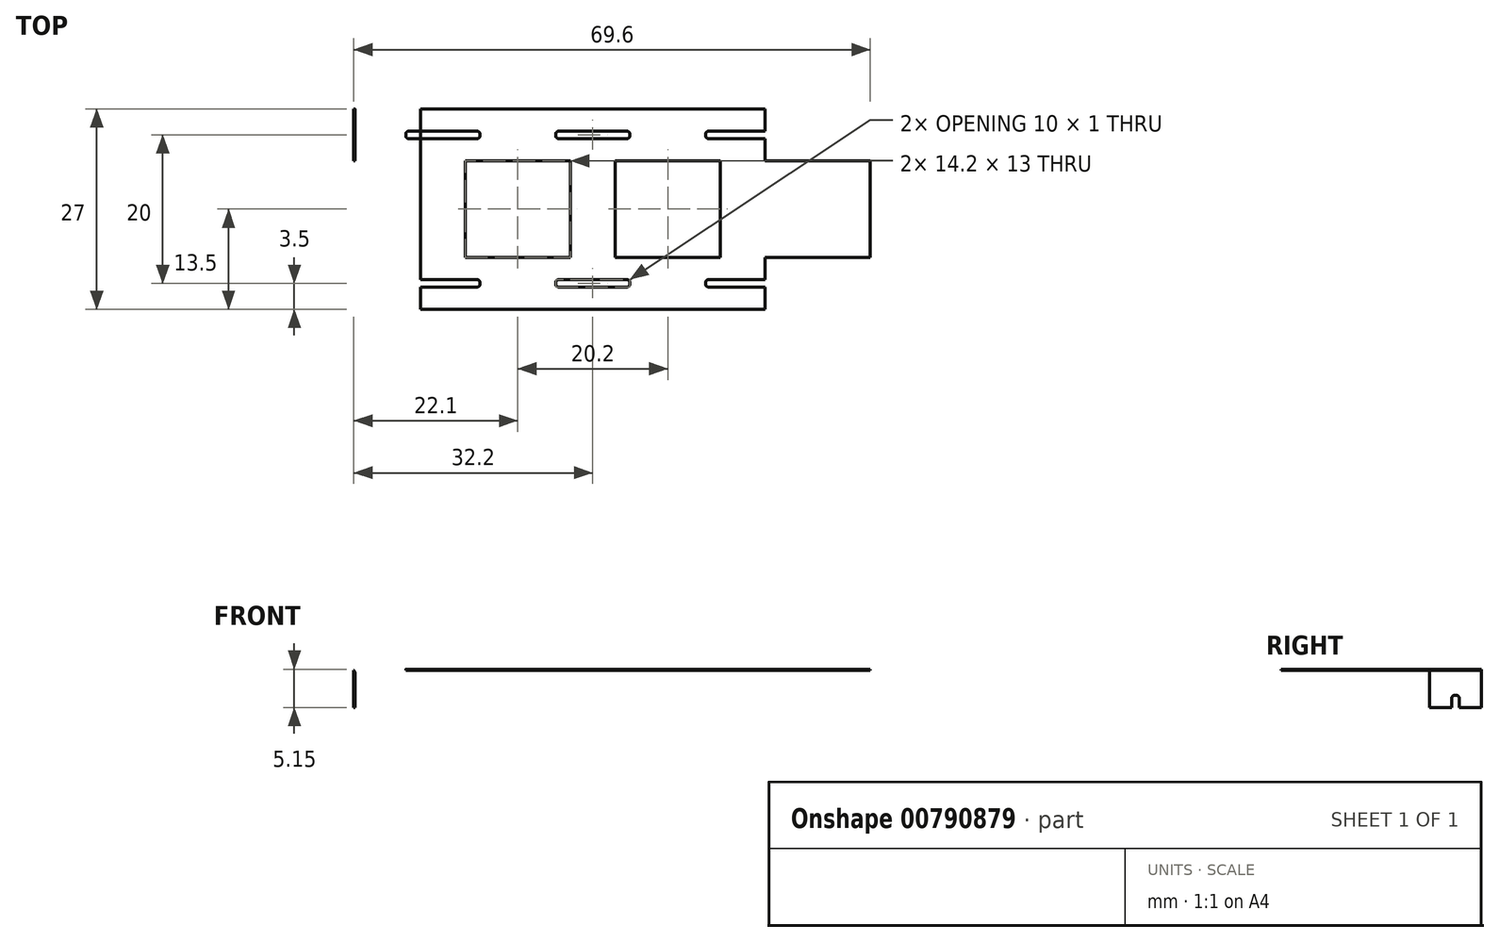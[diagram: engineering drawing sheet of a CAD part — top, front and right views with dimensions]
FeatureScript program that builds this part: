
annotation { "Feature Type Name" : "Feature", "Feature Type Description" : "" }
export const myFeature = defineFeature(function(context is Context, id is Id, definition is map)
    precondition{}
    {
        {
            var Q0;
            Q0=qCreatedBy(makeId("Top.planeOp"),FACE);
            var sketch = newSketch(context, id + "F0", { "sketchPlane" : qUnion([Q0])});
            skLineSegment(sketch, "E0.bottom", {"start": v(7.1, 6.5) * mm, "end": v(-7.1, 6.5) * mm});
            skLineSegment(sketch, "E0.top", {"start": v(7.1, -6.5) * mm, "end": v(-7.1, -6.5) * mm});
            skLineSegment(sketch, "E0.left", {"start": v(7.1, 6.5) * mm, "end": v(7.1, -6.5) * mm});
            skLineSegment(sketch, "E0.right", {"start": v(-7.1, 6.5) * mm, "end": v(-7.1, -6.5) * mm});
            skPoint(sketch, "E0.middle", {"position": v(0, 0) * mm});
            skLineSegment(sketch, "E1", {"start": v(13.1, 13.5) * mm, "end": v(13.1, 10.5) * mm});
            skLineSegment(sketch, "E2", {"start": v(13.1, 13.5) * mm, "end": v(-7.1, 13.5) * mm});
            skLineSegment(sketch, "E3.bottom", {"start": v(5.5, 9.5) * mm, "end": v(14.7, 9.5) * mm});
            skLineSegment(sketch, "E3.top", {"start": v(5.5, 10.5) * mm, "end": v(14.7, 10.5) * mm});
            skLineSegment(sketch, "E3.left", {"start": v(5.1, 9.9) * mm, "end": v(5.1, 10.1) * mm});
            skLineSegment(sketch, "E3.right", {"start": v(15.1, 9.9) * mm, "end": v(15.1, 10.1) * mm});
            skPoint(sketch, "E3.middle", {"position": v(10.1, 10) * mm});
            skPoint(sketch, "E4.visualSharp", {"position": v(5.1, 10.5) * mm});
            skArc(sketch, "E4.filletArc", {"start": v(5.5, 10.5) * mm, "mid": v(5.22, 10.38) * mm, "end": v(5.1, 10.1) * mm});
            skPoint(sketch, "E5.visualSharp", {"position": v(5.1, 9.5) * mm});
            skArc(sketch, "E5.filletArc", {"start": v(5.1, 9.9) * mm, "mid": v(5.22, 9.62) * mm, "end": v(5.5, 9.5) * mm});
            skPoint(sketch, "E6.visualSharp", {"position": v(15.1, 10.5) * mm});
            skArc(sketch, "E6.filletArc", {"start": v(15.1, 10.1) * mm, "mid": v(14.98, 10.38) * mm, "end": v(14.7, 10.5) * mm});
            skPoint(sketch, "E7.visualSharp", {"position": v(15.1, 9.5) * mm});
            skArc(sketch, "E7.filletArc", {"start": v(14.7, 9.5) * mm, "mid": v(14.98, 9.62) * mm, "end": v(15.1, 9.9) * mm});
            skLineSegment(sketch, "E8.trimOffspring", {"start": v(13.1, 9.5) * mm, "end": v(13.1, 0) * mm});
            skArc(sketch, "E9.MirrorCS", {"start": v(-5.5, 10.5) * mm, "mid": v(-5.22, 10.38) * mm, "end": v(-5.1, 10.1) * mm});
            skArc(sketch, "E10.MirrorCS", {"start": v(-15.1, 10.1) * mm, "mid": v(-14.98, 10.38) * mm, "end": v(-14.7, 10.5) * mm});
            skLineSegment(sketch, "E11.MirrorCS", {"start": v(-15.1, 9.9) * mm, "end": v(-15.1, 10.1) * mm});
            skArc(sketch, "E12.MirrorCS", {"start": v(-14.7, 9.5) * mm, "mid": v(-14.98, 9.62) * mm, "end": v(-15.1, 9.9) * mm});
            skArc(sketch, "E13.MirrorCS", {"start": v(-5.1, 9.9) * mm, "mid": v(-5.22, 9.62) * mm, "end": v(-5.5, 9.5) * mm});
            skLineSegment(sketch, "E14.MirrorCS", {"start": v(-5.1, 9.9) * mm, "end": v(-5.1, 10.1) * mm});
            skPoint(sketch, "E15.MirrorP", {"position": v(-5.1, 9.5) * mm});
            skLineSegment(sketch, "E16.MirrorCS", {"start": v(-5.5, 10.5) * mm, "end": v(-14.7, 10.5) * mm});
            skPoint(sketch, "E17.MirrorP", {"position": v(-10.1, 10) * mm});
            skLineSegment(sketch, "E18.MirrorCS", {"start": v(-5.5, 9.5) * mm, "end": v(-14.7, 9.5) * mm});
            skPoint(sketch, "E19.MirrorP", {"position": v(-15.1, 10.5) * mm});
            skLineSegment(sketch, "E20.MirrorCS", {"start": v(-13.1, 9.5) * mm, "end": v(-13.1, 0) * mm});
            skPoint(sketch, "E21.MirrorP", {"position": v(-5.1, 10.5) * mm});
            skLineSegment(sketch, "E22.MirrorCS", {"start": v(-13.1, 13.5) * mm, "end": v(-13.1, 10.5) * mm});
            skPoint(sketch, "E23.MirrorP", {"position": v(-15.1, 9.5) * mm});
            skLineSegment(sketch, "E24", {"start": v(-13.1, 13.5) * mm, "end": v(-7.1, 13.5) * mm});
            skLineSegment(sketch, "E25.bottom", {"start": v(-13.1, 13.5) * mm, "end": v(-22.1, 13.5) * mm});
            skLineSegment(sketch, "E25.top", {"start": v(-13.1, 6.5) * mm, "end": v(-22.1, 6.5) * mm});
            skLineSegment(sketch, "E25.left", {"start": v(-13.1, 13.5) * mm, "end": v(-13.1, 6.5) * mm});
            skLineSegment(sketch, "E25.right", {"start": v(-22.1, 13.5) * mm, "end": v(-22.1, 6.5) * mm});
            skArc(sketch, "E26.MirrorCS", {"start": v(14.7, -9.5) * mm, "mid": v(14.98, -9.62) * mm, "end": v(15.1, -9.9) * mm});
            skLineSegment(sketch, "E27.MirrorCS", {"start": v(15.1, -9.9) * mm, "end": v(15.1, -10.1) * mm});
            skArc(sketch, "E28.MirrorCS", {"start": v(15.1, -10.1) * mm, "mid": v(14.98, -10.38) * mm, "end": v(14.7, -10.5) * mm});
            skLineSegment(sketch, "E29.MirrorCS", {"start": v(13.1, -13.5) * mm, "end": v(13.1, -10.5) * mm});
            skLineSegment(sketch, "E30.MirrorCS", {"start": v(13.1, -9.5) * mm, "end": v(13.1, 0) * mm});
            skLineSegment(sketch, "E31.MirrorCS", {"start": v(13.1, -13.5) * mm, "end": v(-7.1, -13.5) * mm});
            skLineSegment(sketch, "E32.MirrorCS", {"start": v(5.5, -10.5) * mm, "end": v(14.7, -10.5) * mm});
            skPoint(sketch, "E33.MirrorP", {"position": v(15.1, -9.5) * mm});
            skPoint(sketch, "E34.MirrorP", {"position": v(15.1, -10.5) * mm});
            skPoint(sketch, "E35.MirrorP", {"position": v(10.1, -10) * mm});
            skLineSegment(sketch, "E36.MirrorCS", {"start": v(5.5, -9.5) * mm, "end": v(14.7, -9.5) * mm});
            skLineSegment(sketch, "E37.MirrorCS", {"start": v(5.1, -9.9) * mm, "end": v(5.1, -10.1) * mm});
            skArc(sketch, "E38.MirrorCS", {"start": v(5.1, -9.9) * mm, "mid": v(5.22, -9.62) * mm, "end": v(5.5, -9.5) * mm});
            skArc(sketch, "E39.MirrorCS", {"start": v(5.5, -10.5) * mm, "mid": v(5.22, -10.38) * mm, "end": v(5.1, -10.1) * mm});
            skPoint(sketch, "E40.MirrorP", {"position": v(5.1, -10.5) * mm});
            skPoint(sketch, "E41.MirrorP", {"position": v(5.1, -9.5) * mm});
            skArc(sketch, "E42.MirrorCS", {"start": v(-5.1, -9.9) * mm, "mid": v(-5.22, -9.62) * mm, "end": v(-5.5, -9.5) * mm});
            skArc(sketch, "E43.MirrorCS", {"start": v(-5.5, -10.5) * mm, "mid": v(-5.22, -10.38) * mm, "end": v(-5.1, -10.1) * mm});
            skLineSegment(sketch, "E44.MirrorCS", {"start": v(-5.1, -9.9) * mm, "end": v(-5.1, -10.1) * mm});
            skPoint(sketch, "E45.MirrorP", {"position": v(-5.1, -10.5) * mm});
            skLineSegment(sketch, "E46.MirrorCS", {"start": v(-5.5, -10.5) * mm, "end": v(-13.1, -10.5) * mm});
            skPoint(sketch, "E47.MirrorP", {"position": v(-10.1, -10) * mm});
            skPoint(sketch, "E48.MirrorP", {"position": v(-5.1, -9.5) * mm});
            skLineSegment(sketch, "E49.MirrorCS", {"start": v(-5.5, -9.5) * mm, "end": v(-13.1, -9.5) * mm});
            skLineSegment(sketch, "E50.MirrorCS", {"start": v(-13.1, -13.5) * mm, "end": v(-13.1, -10.5) * mm});
            skLineSegment(sketch, "E51.MirrorCS", {"start": v(-13.1, -13.5) * mm, "end": v(-7.1, -13.5) * mm});
            skLineSegment(sketch, "E52.MirrorCS", {"start": v(-13.1, -9.5) * mm, "end": v(-13.1, 0) * mm});
            skLineSegment(sketch, "E53.direction1", {"start": v(-7.1, -13.5) * mm, "end": v(13.1, -13.5) * mm, "construction": true});
            skPoint(sketch, "E54.orphan", {"position": v(-14.7, -9.5) * mm});
            skPoint(sketch, "E55.orphan", {"position": v(-14.7, -10.5) * mm});
            skLineSegment(sketch, "E56.trimOffspring", {"start": v(-13.1, -9.5) * mm, "end": v(-13.1, -6.5) * mm});
            skLineSegment(sketch, "E57.0.1.0", {"start": v(33.3, 9.5) * mm, "end": v(33.3, 0) * mm});
            skPoint(sketch, "E57.3.1.0", {"position": v(25.3, -9.5) * mm});
            skLineSegment(sketch, "E57.4.1.0", {"start": v(33.3, -9.5) * mm, "end": v(33.3, 0) * mm});
            skLineSegment(sketch, "E57.7.1.0", {"start": v(33.3, -13.5) * mm, "end": v(13.1, -13.5) * mm});
            skPoint(sketch, "E57.10.1.0", {"position": v(20.2, 0) * mm});
            skLineSegment(sketch, "E57.11.1.0", {"start": v(27.3, 6.5) * mm, "end": v(27.3, -6.5) * mm});
            skLineSegment(sketch, "E57.14.1.0", {"start": v(27.3, -6.5) * mm, "end": v(13.1, -6.5) * mm});
            skLineSegment(sketch, "E57.17.1.0", {"start": v(27.3, 6.5) * mm, "end": v(13.1, 6.5) * mm});
            skPoint(sketch, "E57.20.1.0", {"position": v(30.3, 10) * mm});
            skPoint(sketch, "E57.21.1.0", {"position": v(25.3, 10.5) * mm});
            skLineSegment(sketch, "E57.22.1.0", {"start": v(25.7, -9.5) * mm, "end": v(34.9, -9.5) * mm});
            skPoint(sketch, "E57.25.1.0", {"position": v(30.3, -10) * mm});
            skPoint(sketch, "E57.26.1.0", {"position": v(25.3, -10.5) * mm});
            skLineSegment(sketch, "E57.27.1.0", {"start": v(25.7, 10.5) * mm, "end": v(34.9, 10.5) * mm});
            skPoint(sketch, "E57.30.1.0", {"position": v(25.3, 9.5) * mm});
            skLineSegment(sketch, "E57.31.1.0", {"start": v(33.3, 13.5) * mm, "end": v(33.3, 10.5) * mm});
            skLineSegment(sketch, "E57.34.1.0", {"start": v(33.3, -13.5) * mm, "end": v(33.3, -10.5) * mm});
            skLineSegment(sketch, "E57.37.1.0", {"start": v(25.7, 9.5) * mm, "end": v(34.9, 9.5) * mm});
            skLineSegment(sketch, "E57.40.1.0", {"start": v(33.3, 13.5) * mm, "end": v(13.1, 13.5) * mm});
            skPoint(sketch, "E57.43.1.0", {"position": v(35.3, -10.5) * mm});
            skLineSegment(sketch, "E57.44.1.0", {"start": v(25.7, -10.5) * mm, "end": v(34.9, -10.5) * mm});
            skPoint(sketch, "E57.47.1.0", {"position": v(35.3, 9.5) * mm});
            skPoint(sketch, "E57.48.1.0", {"position": v(35.3, 10.5) * mm});
            skPoint(sketch, "E57.49.1.0", {"position": v(35.3, -9.5) * mm});
            skPoint(sketch, "E57.50.1.0", {"position": v(20.2, 0) * mm});
            skArc(sketch, "E57.51.1.0", {"start": v(35.3, 10.1) * mm, "mid": v(35.18, 10.38) * mm, "end": v(34.9, 10.5) * mm});
            skArc(sketch, "E57.55.1.0", {"start": v(34.9, 9.5) * mm, "mid": v(35.18, 9.62) * mm, "end": v(35.3, 9.9) * mm});
            skArc(sketch, "E57.59.1.0", {"start": v(25.3, 9.9) * mm, "mid": v(25.42, 9.62) * mm, "end": v(25.7, 9.5) * mm});
            skArc(sketch, "E57.63.1.0", {"start": v(25.7, 10.5) * mm, "mid": v(25.42, 10.38) * mm, "end": v(25.3, 10.1) * mm});
            skLineSegment(sketch, "E57.67.1.0", {"start": v(35.3, 9.9) * mm, "end": v(35.3, 10.1) * mm});
            skLineSegment(sketch, "E57.70.1.0", {"start": v(25.3, 9.9) * mm, "end": v(25.3, 10.1) * mm});
            skArc(sketch, "E57.73.1.0", {"start": v(25.7, -10.5) * mm, "mid": v(25.42, -10.38) * mm, "end": v(25.3, -10.1) * mm});
            skArc(sketch, "E57.77.1.0", {"start": v(25.3, -9.9) * mm, "mid": v(25.42, -9.62) * mm, "end": v(25.7, -9.5) * mm});
            skArc(sketch, "E57.81.1.0", {"start": v(34.9, -9.5) * mm, "mid": v(35.18, -9.62) * mm, "end": v(35.3, -9.9) * mm});
            skArc(sketch, "E57.85.1.0", {"start": v(35.3, -10.1) * mm, "mid": v(35.18, -10.38) * mm, "end": v(34.9, -10.5) * mm});
            skLineSegment(sketch, "E57.89.1.0", {"start": v(35.3, -9.9) * mm, "end": v(35.3, -10.1) * mm});
            skLineSegment(sketch, "E57.92.1.0", {"start": v(25.3, -9.9) * mm, "end": v(25.3, -10.1) * mm});
            skLineSegment(sketch, "E57.95.1.0", {"start": v(13.1, 6.5) * mm, "end": v(13.1, -6.5) * mm});
            skLineSegment(sketch, "E58.0.2.0", {"start": v(53.5, 9.5) * mm, "end": v(53.5, 0) * mm});
            skPoint(sketch, "E58.3.2.0", {"position": v(45.5, -9.5) * mm});
            skLineSegment(sketch, "E58.4.2.0", {"start": v(53.5, -9.5) * mm, "end": v(53.5, 0) * mm});
            skLineSegment(sketch, "E58.7.2.0", {"start": v(53.5, -13.5) * mm, "end": v(33.3, -13.5) * mm});
            skPoint(sketch, "E58.10.2.0", {"position": v(40.4, 0) * mm});
            skLineSegment(sketch, "E58.11.2.0", {"start": v(47.5, 6.5) * mm, "end": v(47.5, -6.5) * mm});
            skLineSegment(sketch, "E58.14.2.0", {"start": v(47.5, -6.5) * mm, "end": v(33.3, -6.5) * mm});
            skLineSegment(sketch, "E58.17.2.0", {"start": v(47.5, 6.5) * mm, "end": v(33.3, 6.5) * mm});
            skPoint(sketch, "E58.20.2.0", {"position": v(50.5, 10) * mm});
            skPoint(sketch, "E58.21.2.0", {"position": v(45.5, 10.5) * mm});
            skLineSegment(sketch, "E58.22.2.0", {"start": v(45.9, -9.5) * mm, "end": v(55.1, -9.5) * mm});
            skPoint(sketch, "E58.25.2.0", {"position": v(50.5, -10) * mm});
            skPoint(sketch, "E58.26.2.0", {"position": v(45.5, -10.5) * mm});
            skLineSegment(sketch, "E58.27.2.0", {"start": v(45.9, 10.5) * mm, "end": v(55.1, 10.5) * mm});
            skPoint(sketch, "E58.30.2.0", {"position": v(45.5, 9.5) * mm});
            skLineSegment(sketch, "E58.31.2.0", {"start": v(53.5, 13.5) * mm, "end": v(53.5, 10.5) * mm});
            skLineSegment(sketch, "E58.34.2.0", {"start": v(53.5, -13.5) * mm, "end": v(53.5, -10.5) * mm});
            skLineSegment(sketch, "E58.37.2.0", {"start": v(45.9, 9.5) * mm, "end": v(55.1, 9.5) * mm});
            skLineSegment(sketch, "E58.40.2.0", {"start": v(53.5, 13.5) * mm, "end": v(33.3, 13.5) * mm});
            skPoint(sketch, "E58.43.2.0", {"position": v(55.5, -10.5) * mm});
            skLineSegment(sketch, "E58.44.2.0", {"start": v(45.9, -10.5) * mm, "end": v(55.1, -10.5) * mm});
            skPoint(sketch, "E58.47.2.0", {"position": v(55.5, 9.5) * mm});
            skPoint(sketch, "E58.48.2.0", {"position": v(55.5, 10.5) * mm});
            skPoint(sketch, "E58.49.2.0", {"position": v(55.5, -9.5) * mm});
            skPoint(sketch, "E58.50.2.0", {"position": v(40.4, 0) * mm});
            skArc(sketch, "E58.51.2.0", {"start": v(55.5, 10.1) * mm, "mid": v(55.38, 10.38) * mm, "end": v(55.1, 10.5) * mm});
            skArc(sketch, "E58.55.2.0", {"start": v(55.1, 9.5) * mm, "mid": v(55.38, 9.62) * mm, "end": v(55.5, 9.9) * mm});
            skArc(sketch, "E58.59.2.0", {"start": v(45.5, 9.9) * mm, "mid": v(45.62, 9.62) * mm, "end": v(45.9, 9.5) * mm});
            skArc(sketch, "E58.63.2.0", {"start": v(45.9, 10.5) * mm, "mid": v(45.62, 10.38) * mm, "end": v(45.5, 10.1) * mm});
            skLineSegment(sketch, "E58.67.2.0", {"start": v(55.5, 9.9) * mm, "end": v(55.5, 10.1) * mm});
            skLineSegment(sketch, "E58.70.2.0", {"start": v(45.5, 9.9) * mm, "end": v(45.5, 10.1) * mm});
            skArc(sketch, "E58.73.2.0", {"start": v(45.9, -10.5) * mm, "mid": v(45.62, -10.38) * mm, "end": v(45.5, -10.1) * mm});
            skArc(sketch, "E58.77.2.0", {"start": v(45.5, -9.9) * mm, "mid": v(45.62, -9.62) * mm, "end": v(45.9, -9.5) * mm});
            skArc(sketch, "E58.81.2.0", {"start": v(55.1, -9.5) * mm, "mid": v(55.38, -9.62) * mm, "end": v(55.5, -9.9) * mm});
            skArc(sketch, "E58.85.2.0", {"start": v(55.5, -10.1) * mm, "mid": v(55.38, -10.38) * mm, "end": v(55.1, -10.5) * mm});
            skLineSegment(sketch, "E58.89.2.0", {"start": v(55.5, -9.9) * mm, "end": v(55.5, -10.1) * mm});
            skLineSegment(sketch, "E58.92.2.0", {"start": v(45.5, -9.9) * mm, "end": v(45.5, -10.1) * mm});
            skLineSegment(sketch, "E58.95.2.0", {"start": v(33.3, 6.5) * mm, "end": v(33.3, -6.5) * mm});
            skSolve(sketch);
        }
        {
            var Q0;
            {var subQ5=sQuery(id+"F0.wireOp",EDGE,"E10.MirrorCS");Q0=makeQuery(id+"F0.imprint","IMPRINT",FACE,{"disambiguationData":[TD([[makeQuery(id+"F0.imprint","IMPRINT",EDGE,{"derivedFrom":subQ5}),1.0]])]});}
            var Q1;
            {var subQ14=sQuery(id+"F0.wireOp",EDGE,"E53.1.0.0");Q1=makeQuery(id+"F0.imprint","IMPRINT",FACE,{"disambiguationData":[TD([[makeQuery(id+"F0.imprint","IMPRINT",EDGE,{"derivedFrom":subQ14}),1.0]])]});}
            var Q2;
            Q2=makeQuery(id+"F0.imprint","IMPRINT",FACE,{"disambiguationData":[TD([[makeQuery(id+"F0.imprint","IMPRINT",EDGE,{"derivedFrom":sQuery(id+"F0.wireOp",EDGE,"E0.bottom")}),-1.0]])]});
            var Q3;
            {var subQ5=sQuery(id+"F0.wireOp",EDGE,"E1");Q3=makeQuery(id+"F0.imprint","IMPRINT",FACE,{"disambiguationData":[TD([[makeQuery(id+"F0.imprint","IMPRINT",EDGE,{"derivedFrom":subQ5}),1.0]])]});}
            var Q4;
            {var subQ14=sQuery(id+"F0.wireOp",EDGE,"E57.0.1.0");Q4=makeQuery(id+"F0.imprint","IMPRINT",FACE,{"disambiguationData":[TD([[makeQuery(id+"F0.imprint","IMPRINT",EDGE,{"derivedFrom":subQ14}),1.0]])]});}
            extrude(context, id + "F1", {"entities" : qUnion([Q0, Q1, Q2, Q3, Q4]), "depth" : 0.15 * mm, "offsetDistance" : 25 * mm});
        }
        {
            var Q0;
            Q0=makeQuery(id+"F1.opExtrude","CAP_FACE",FACE,{"disambiguationData":[OSD([sQuery(id+"F0.wireOp",EDGE,"E0.bottom"),sQuery(id+"F0.wireOp",EDGE,"E0.top"),sQuery(id+"F0.wireOp",EDGE,"E0.left"),sQuery(id+"F0.wireOp",EDGE,"E0.right"),sQuery(id+"F0.wireOp",EDGE,"E2"),sQuery(id+"F0.wireOp",EDGE,"E3.bottom"),sQuery(id+"F0.wireOp",EDGE,"E3.top"),sQuery(id+"F0.wireOp",EDGE,"E3.left"),sQuery(id+"F0.wireOp",EDGE,"E3.right"),sQuery(id+"F0.wireOp",EDGE,"E4.filletArc"),sQuery(id+"F0.wireOp",EDGE,"E5.filletArc"),sQuery(id+"F0.wireOp",EDGE,"E6.filletArc"),sQuery(id+"F0.wireOp",EDGE,"E7.filletArc"),sQuery(id+"F0.wireOp",EDGE,"E9.MirrorCS"),sQuery(id+"F0.wireOp",EDGE,"E10.MirrorCS"),sQuery(id+"F0.wireOp",EDGE,"E11.MirrorCS"),sQuery(id+"F0.wireOp",EDGE,"E12.MirrorCS"),sQuery(id+"F0.wireOp",EDGE,"E13.MirrorCS"),sQuery(id+"F0.wireOp",EDGE,"E14.MirrorCS"),sQuery(id+"F0.wireOp",EDGE,"E16.MirrorCS"),sQuery(id+"F0.wireOp",EDGE,"E18.MirrorCS"),sQuery(id+"F0.wireOp",EDGE,"E20.MirrorCS"),sQuery(id+"F0.wireOp",EDGE,"E24"),sQuery(id+"F0.wireOp",EDGE,"E25.bottom"),sQuery(id+"F0.wireOp",EDGE,"E25.top"),sQuery(id+"F0.wireOp",EDGE,"E25.right"),sQuery(id+"F0.wireOp",EDGE,"E26.MirrorCS"),sQuery(id+"F0.wireOp",EDGE,"E27.MirrorCS"),sQuery(id+"F0.wireOp",EDGE,"E28.MirrorCS"),sQuery(id+"F0.wireOp",EDGE,"E31.MirrorCS"),sQuery(id+"F0.wireOp",EDGE,"E32.MirrorCS"),sQuery(id+"F0.wireOp",EDGE,"E36.MirrorCS"),sQuery(id+"F0.wireOp",EDGE,"E37.MirrorCS"),sQuery(id+"F0.wireOp",EDGE,"E38.MirrorCS"),sQuery(id+"F0.wireOp",EDGE,"E39.MirrorCS"),sQuery(id+"F0.wireOp",EDGE,"E42.MirrorCS"),sQuery(id+"F0.wireOp",EDGE,"E43.MirrorCS"),sQuery(id+"F0.wireOp",EDGE,"E44.MirrorCS"),sQuery(id+"F0.wireOp",EDGE,"E46.MirrorCS"),sQuery(id+"F0.wireOp",EDGE,"E49.MirrorCS"),sQuery(id+"F0.wireOp",EDGE,"E50.MirrorCS"),sQuery(id+"F0.wireOp",EDGE,"E51.MirrorCS"),sQuery(id+"F0.wireOp",EDGE,"E52.MirrorCS"),sQuery(id+"F0.wireOp",EDGE,"E53.1.0.3"),sQuery(id+"F0.wireOp",EDGE,"E53.1.0.5"),sQuery(id+"F0.wireOp",EDGE,"E53.1.0.6"),sQuery(id+"F0.wireOp",EDGE,"E53.1.0.7"),sQuery(id+"F0.wireOp",EDGE,"E53.1.0.10"),sQuery(id+"F0.wireOp",EDGE,"E53.1.0.13"),sQuery(id+"F0.wireOp",EDGE,"E53.1.0.17"),sQuery(id+"F0.wireOp",EDGE,"E53.1.0.18"),sQuery(id+"F0.wireOp",EDGE,"E53.1.0.20"),sQuery(id+"F0.wireOp",EDGE,"E53.1.0.25"),sQuery(id+"F0.wireOp",EDGE,"E53.1.0.26"),sQuery(id+"F0.wireOp",EDGE,"E53.1.0.27"),sQuery(id+"F0.wireOp",EDGE,"E53.1.0.28"),sQuery(id+"F0.wireOp",EDGE,"E53.1.0.29"),sQuery(id+"F0.wireOp",EDGE,"E53.1.0.30"),sQuery(id+"F0.wireOp",EDGE,"E53.1.0.31"),sQuery(id+"F0.wireOp",EDGE,"E53.1.0.32"),sQuery(id+"F0.wireOp",EDGE,"E53.1.0.33"),sQuery(id+"F0.wireOp",EDGE,"E53.1.0.34"),sQuery(id+"F0.wireOp",EDGE,"E53.1.0.35"),sQuery(id+"F0.wireOp",EDGE,"E53.1.0.36"),sQuery(id+"F0.wireOp",EDGE,"E53.1.0.37"),sQuery(id+"F0.wireOp",EDGE,"E53.2.0.0"),sQuery(id+"F0.wireOp",EDGE,"E53.2.0.2"),sQuery(id+"F0.wireOp",EDGE,"E53.2.0.3"),sQuery(id+"F0.wireOp",EDGE,"E53.2.0.5"),sQuery(id+"F0.wireOp",EDGE,"E53.2.0.6"),sQuery(id+"F0.wireOp",EDGE,"E53.2.0.7"),sQuery(id+"F0.wireOp",EDGE,"E53.2.0.10"),sQuery(id+"F0.wireOp",EDGE,"E53.2.0.13"),sQuery(id+"F0.wireOp",EDGE,"E53.2.0.15"),sQuery(id+"F0.wireOp",EDGE,"E53.2.0.16"),sQuery(id+"F0.wireOp",EDGE,"E53.2.0.17"),sQuery(id+"F0.wireOp",EDGE,"E53.2.0.18"),sQuery(id+"F0.wireOp",EDGE,"E53.2.0.20"),sQuery(id+"F0.wireOp",EDGE,"E53.2.0.27"),sQuery(id+"F0.wireOp",EDGE,"E53.2.0.28"),sQuery(id+"F0.wireOp",EDGE,"E53.2.0.30"),sQuery(id+"F0.wireOp",EDGE,"E53.2.0.31"),sQuery(id+"F0.wireOp",EDGE,"E53.2.0.32"),sQuery(id+"F0.wireOp",EDGE,"E53.2.0.36"),sQuery(id+"F0.wireOp",EDGE,"E53.2.0.37"),sQuery(id+"F0.wireOp",EDGE,"E56.trimOffspring")])],"isStart":true});
            var sketch = newSketch(context, id + "F2", { "sketchPlane" : qUnion([Q0])});
            skLineSegment(sketch, "E59.bottom", {"start": v(-22.1, -13.5) * mm, "end": v(-21.95, -13.5) * mm});
            skLineSegment(sketch, "E59.top", {"start": v(-22.1, -6.5) * mm, "end": v(-21.95, -6.5) * mm});
            skLineSegment(sketch, "E59.left", {"start": v(-22.1, -13.5) * mm, "end": v(-22.1, -6.5) * mm});
            skLineSegment(sketch, "E59.right", {"start": v(-21.95, -13.5) * mm, "end": v(-21.95, -6.5) * mm});
            skSolve(sketch);
        }
        {
            var Q0;
            Q0=qSketchRegion(id+"F2",true);
            extrude(context, id + "F3", {"entities" : qUnion([Q0]), "operationType" : NewBodyOperationType.ADD, "depth" : 5 * mm, "offsetDistance" : 25 * mm});
        }
        {
            var Q0;
            Q0=makeQuery(id+"F3.opExtrude","CAP_EDGE",EDGE,{"disambiguationData":[OSD([sQuery(id+"F2.wireOp",EDGE,"E59.right")])],"isStart":true});
            var Q1;
            Q1=makeQuery(id+"F1.opExtrude","CAP_EDGE",EDGE,{"disambiguationData":[OSD([sQuery(id+"F0.wireOp",EDGE,"E25.right")])],"isStart":false});
            fillet(context, id + "F4", {"entities" : qUnion([Q0, Q1]), "radius" : 0.5 * mm, "tangentPropagation" : true, "allowEdgeOverflow" : false});
        }
        {
            var Q0;
            Q0=makeQuery(id+"F3.boolean.opBoolean","MERGE",FACE,{"derivedFrom":[makeQuery(id+"F1.opExtrude","SWEPT_FACE",FACE,{"disambiguationData":[OSD([sQuery(id+"F0.wireOp",EDGE,"E25.right")])]}),makeQuery(id+"F3.opExtrude","SWEPT_FACE",FACE,{"disambiguationData":[OSD([sQuery(id+"F2.wireOp",EDGE,"E59.left")])]})]});
            var sketch = newSketch(context, id + "F5", { "sketchPlane" : qUnion([Q0])});
            skLineSegment(sketch, "E60", {"start": v(-10, -0.35) * mm, "end": v(-10, -3.35) * mm});
            skLineSegment(sketch, "E61", {"start": v(-10, -3.35) * mm, "end": v(-9.9, -3.35) * mm});
            skLineSegment(sketch, "E62", {"start": v(-9.5, -3.75) * mm, "end": v(-9.5, -5) * mm});
            skPoint(sketch, "E63.visualSharp", {"position": v(-9.5, -3.35) * mm});
            skArc(sketch, "E63.filletArc", {"start": v(-9.5, -3.75) * mm, "mid": v(-9.62, -3.47) * mm, "end": v(-9.9, -3.35) * mm});
            skPoint(sketch, "E64.MirrorP", {"position": v(-10.5, -3.35) * mm});
            skLineSegment(sketch, "E65.MirrorCS", {"start": v(-10.5, -3.75) * mm, "end": v(-10.5, -5) * mm});
            skArc(sketch, "E66.MirrorCS", {"start": v(-10.5, -3.75) * mm, "mid": v(-10.38, -3.47) * mm, "end": v(-10.1, -3.35) * mm});
            skLineSegment(sketch, "E67.MirrorCS", {"start": v(-10, -3.35) * mm, "end": v(-10.1, -3.35) * mm});
            skSolve(sketch);
        }
        {
            var Q0;
            Q0=makeQuery(id+"F5.imprint","IMPRINT",FACE,{"disambiguationData":[TD([[makeQuery(id+"F5.imprint","IMPRINT",EDGE,{"derivedFrom":sQuery(id+"F5.wireOp",EDGE,"E61")}),-1.0]])]});
            extrude(context, id + "F6", {"entities" : qUnion([Q0]), "operationType" : NewBodyOperationType.REMOVE, "oppositeDirection" : true, "depth" : 25 * mm, "offsetDistance" : 25 * mm});
        }
    });
